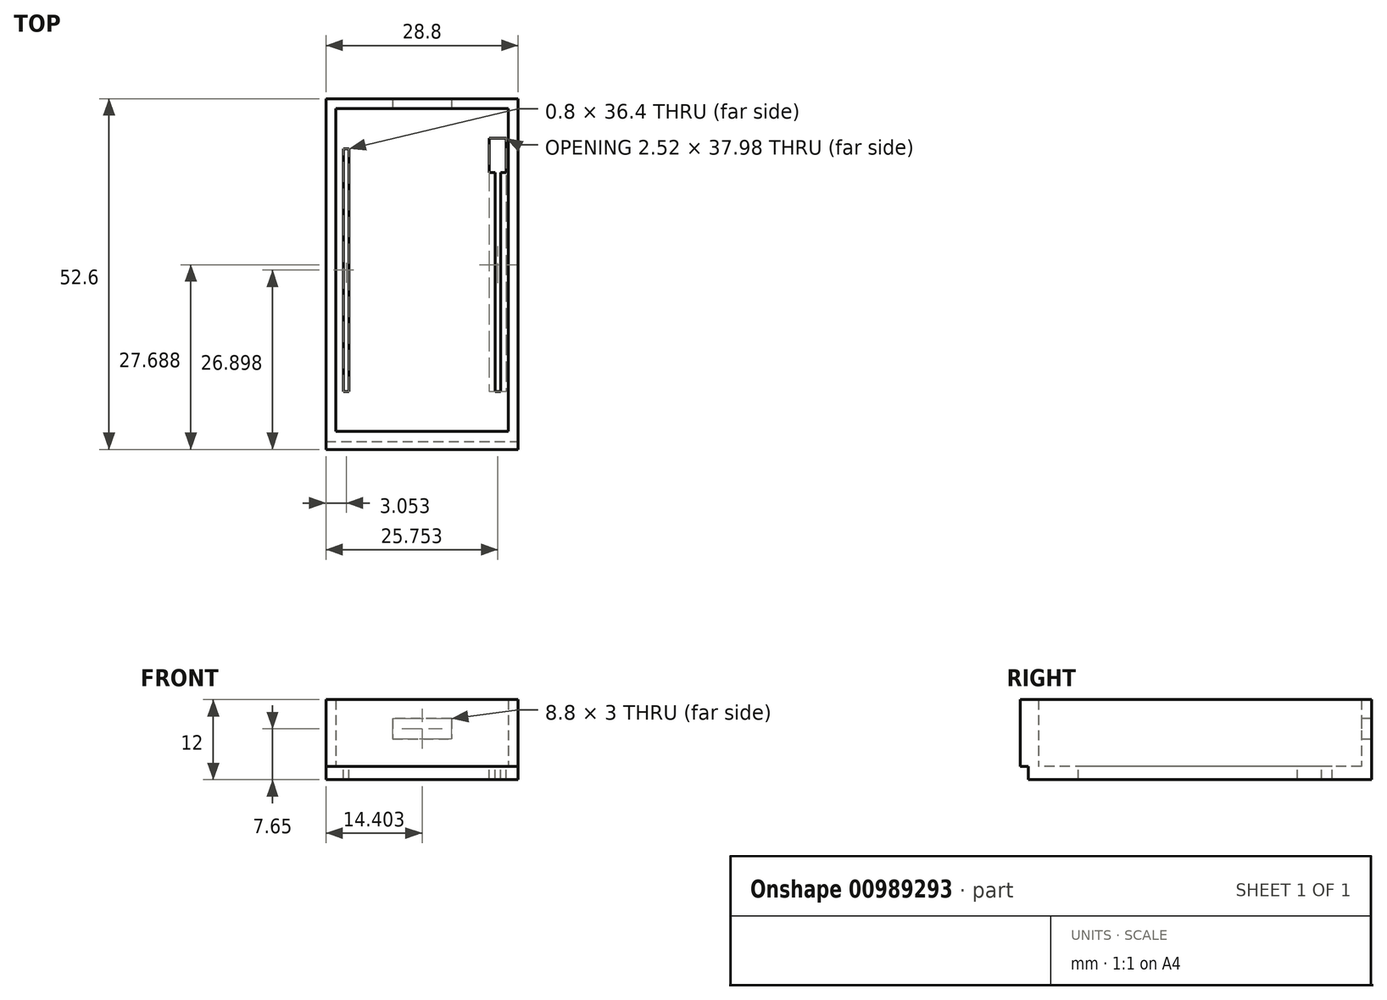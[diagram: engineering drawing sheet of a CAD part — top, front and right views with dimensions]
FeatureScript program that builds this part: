
annotation { "Feature Type Name" : "Feature", "Feature Type Description" : "" }
export const myFeature = defineFeature(function(context is Context, id is Id, definition is map)
    precondition{}
    {
        {
            var Q0;
            Q0=qCreatedBy(makeId("Top.planeOp"),FACE);
            var sketch = newSketch(context, id + "F0", { "sketchPlane" : qUnion([Q0])});
            skLineSegment(sketch, "E0.bottom", {"start": v(-15.5, 31.2) * mm, "end": v(10.3, 31.2) * mm});
            skLineSegment(sketch, "E0.top", {"start": v(-15.5, -17.2) * mm, "end": v(10.3, -17.2) * mm});
            skLineSegment(sketch, "E0.left", {"start": v(-15.5, 31.2) * mm, "end": v(-15.5, -17.2) * mm});
            skLineSegment(sketch, "E0.right", {"start": v(10.3, 31.2) * mm, "end": v(10.3, -17.2) * mm});
            skLineSegment(sketch, "E1.0", {"start": v(-17, 32.7) * mm, "end": v(11.8, 32.7) * mm});
            skLineSegment(sketch, "E1.1", {"start": v(-17, 32.7) * mm, "end": v(-17, -18.7) * mm});
            skLineSegment(sketch, "E1.2", {"start": v(-17, -18.7) * mm, "end": v(11.8, -18.7) * mm});
            skLineSegment(sketch, "E1.3", {"start": v(11.8, 32.7) * mm, "end": v(11.8, -18.7) * mm});
            skPoint(sketch, "E2", {"position": v(-2.6, 31.2) * mm});
            skPoint(sketch, "E3", {"position": v(-2.6, 32.7) * mm});
            skLineSegment(sketch, "E4", {"start": v(-2.6, 32.7) * mm, "end": v(-2.6, 31.2) * mm, "construction": true});
            skPoint(sketch, "E5", {"position": v(-2.6, 31.95) * mm});
            skLineSegment(sketch, "E6.bottom", {"start": v(1.8, 31.2) * mm, "end": v(-7, 31.2) * mm});
            skLineSegment(sketch, "E6.top", {"start": v(1.8, 32.7) * mm, "end": v(-7, 32.7) * mm});
            skLineSegment(sketch, "E6.left", {"start": v(1.8, 31.2) * mm, "end": v(1.8, 32.7) * mm});
            skLineSegment(sketch, "E6.right", {"start": v(-7, 31.2) * mm, "end": v(-7, 32.7) * mm});
            skLineSegment(sketch, "E7", {"start": v(-13.96, 31.2) * mm, "end": v(-13.96, -17.2) * mm, "construction": true});
            skLineSegment(sketch, "E8", {"start": v(8.74, 31.2) * mm, "end": v(8.74, -17.2) * mm, "construction": true});
            skLineSegment(sketch, "E9", {"start": v(-15.5, 31.2) * mm, "end": v(-13.96, 31.2) * mm, "construction": true});
            skLineSegment(sketch, "E10", {"start": v(8.74, 31.2) * mm, "end": v(10.3, 31.2) * mm, "construction": true});
            skPoint(sketch, "E11", {"position": v(-13.96, 7) * mm});
            skPoint(sketch, "E12", {"position": v(8.74, 7) * mm});
            skLineSegment(sketch, "E13.bottom", {"start": v(-14.36, 25.2) * mm, "end": v(-13.56, 25.2) * mm});
            skLineSegment(sketch, "E13.top", {"start": v(-14.36, -11.2) * mm, "end": v(-13.56, -11.2) * mm});
            skLineSegment(sketch, "E13.left", {"start": v(-14.36, 25.2) * mm, "end": v(-14.36, -11.2) * mm});
            skLineSegment(sketch, "E13.right", {"start": v(-13.56, 25.2) * mm, "end": v(-13.56, -11.2) * mm});
            skLineSegment(sketch, "E14.bottom", {"start": v(8.34, 25.2) * mm, "end": v(9.14, 25.2) * mm});
            skLineSegment(sketch, "E14.top", {"start": v(8.34, -11.2) * mm, "end": v(9.14, -11.2) * mm});
            skLineSegment(sketch, "E14.left", {"start": v(8.34, 25.2) * mm, "end": v(8.34, -11.2) * mm});
            skLineSegment(sketch, "E14.right", {"start": v(9.14, 25.2) * mm, "end": v(9.14, -11.2) * mm});
            skPoint(sketch, "E15", {"position": v(-2.6, -18.7) * mm});
            skPoint(sketch, "E16", {"position": v(-13.96, 25.2) * mm});
            skPoint(sketch, "E17", {"position": v(8.74, 25.2) * mm});
            skPoint(sketch, "E18", {"position": v(-13.96, -11.2) * mm});
            skPoint(sketch, "E19", {"position": v(8.74, -11.2) * mm});
            skPoint(sketch, "E20", {"position": v(8.74, 26.78) * mm});
            skPoint(sketch, "E21", {"position": v(8.74, 21.6) * mm});
            skLineSegment(sketch, "E22", {"start": v(8.74, 26.78) * mm, "end": v(7.48, 26.78) * mm});
            skLineSegment(sketch, "E23", {"start": v(7.48, 26.78) * mm, "end": v(8.74, 26.78) * mm});
            skLineSegment(sketch, "E24", {"start": v(8.74, 26.78) * mm, "end": v(10, 26.78) * mm});
            skLineSegment(sketch, "E25.bottom", {"start": v(7.48, 26.78) * mm, "end": v(10, 26.78) * mm});
            skLineSegment(sketch, "E25.top", {"start": v(7.48, 21.6) * mm, "end": v(10, 21.6) * mm});
            skLineSegment(sketch, "E25.left", {"start": v(7.48, 26.78) * mm, "end": v(7.48, 21.6) * mm});
            skLineSegment(sketch, "E25.right", {"start": v(10, 26.78) * mm, "end": v(10, 21.6) * mm});
            skLineSegment(sketch, "E26.top", {"start": v(-17, -19.9) * mm, "end": v(11.8, -19.9) * mm});
            skLineSegment(sketch, "E26.left", {"start": v(-17, -18.7) * mm, "end": v(-17, -19.9) * mm});
            skLineSegment(sketch, "E26.right", {"start": v(11.8, -18.7) * mm, "end": v(11.8, -19.9) * mm});
            skSolve(sketch);
        }
        {
            var Q0;
            Q0=makeQuery(id+"F0.imprint","IMPRINT",FACE,{"disambiguationData":[TD([[makeQuery(id+"F0.imprint","IMPRINT",EDGE,{"derivedFrom":sQuery(id+"F0.wireOp",EDGE,"E0.top")}),-1.0]])]});
            var Q1;
            Q1=makeQuery(id+"F0.imprint","IMPRINT",FACE,{"disambiguationData":[TD([[makeQuery(id+"F0.imprint","IMPRINT",EDGE,{"derivedFrom":sQuery(id+"F0.wireOp",EDGE,"E0.top")}),1.0]])]});
            var Q2;
            {var subQ2=sQuery(id+"F0.wireOp",EDGE,"E6.left");Q2=makeQuery(id+"F0.imprint","IMPRINT",FACE,{"disambiguationData":[TD([[makeQuery(id+"F0.imprint","IMPRINT",EDGE,{"derivedFrom":subQ2}),1.0]])]});}
            extrude(context, id + "F1", {"entities" : qUnion([Q0, Q1, Q2]), "oppositeDirection" : true, "depth" : 2 * mm, "offsetDistance" : 25 * mm});
        }
        {
            var Q0;
            Q0=makeQuery(id+"F0.imprint","IMPRINT",FACE,{"disambiguationData":[TD([[makeQuery(id+"F0.imprint","IMPRINT",EDGE,{"derivedFrom":sQuery(id+"F0.wireOp",EDGE,"E0.top")}),-1.0]])]});
            extrude(context, id + "F2", {"entities" : qUnion([Q0]), "operationType" : NewBodyOperationType.ADD, "depth" : 10 * mm, "offsetDistance" : 25 * mm});
        }
        {
            var Q0;
            {var subQ2=sQuery(id+"F0.wireOp",EDGE,"E6.left");Q0=makeQuery(id+"F0.imprint","IMPRINT",FACE,{"disambiguationData":[TD([[makeQuery(id+"F0.imprint","IMPRINT",EDGE,{"derivedFrom":subQ2}),1.0]])]});}
            extrude(context, id + "F3", {"entities" : qUnion([Q0]), "operationType" : NewBodyOperationType.ADD, "depth" : 4.15 * mm, "offsetDistance" : 25 * mm});
        }
        {
            var Q0;
            Q0=makeQuery(id+"F0.imprint","IMPRINT",FACE,{"disambiguationData":[TD([[makeQuery(id+"F0.imprint","IMPRINT",EDGE,{"derivedFrom":sQuery(id+"F0.wireOp",EDGE,"E13.bottom")}),-1.0]])]});
            var Q1;
            {var subQ0=sQuery(id+"F0.wireOp",EDGE,"E14.bottom");Q1=makeQuery(id+"F0.imprint","IMPRINT",FACE,{"disambiguationData":[TD([[makeQuery(id+"F0.imprint","IMPRINT",EDGE,{"derivedFrom":subQ0}),-1.0]])]});}
            extrude(context, id + "F4", {"entities" : qUnion([Q0, Q1]), "operationType" : NewBodyOperationType.REMOVE, "oppositeDirection" : true, "depth" : 2 * mm, "offsetDistance" : 25 * mm});
        }
        {
            var Q0;
            Q0=makeQuery(id+"F2.opExtrude","SWEPT_FACE",FACE,{"disambiguationData":[OSD([sQuery(id+"F0.wireOp",EDGE,"E6.right")])]});
            var sketch = newSketch(context, id + "F5", { "sketchPlane" : qUnion([Q0])});
            skPoint(sketch, "E27", {"position": v(32.7, 4.15) * mm});
            skPoint(sketch, "E28", {"position": v(31.2, 4.15) * mm});
            skPoint(sketch, "E29", {"position": v(31.2, 7.15) * mm});
            skPoint(sketch, "E30", {"position": v(32.7, 7.15) * mm});
            skLineSegment(sketch, "E31", {"start": v(31.2, 4.15) * mm, "end": v(31.2, 7.15) * mm});
            skLineSegment(sketch, "E32", {"start": v(32.7, 7.15) * mm, "end": v(31.2, 7.15) * mm});
            skLineSegment(sketch, "E33", {"start": v(32.7, 4.15) * mm, "end": v(32.7, 7.15) * mm});
            skLineSegment(sketch, "E34", {"start": v(32.7, 4.15) * mm, "end": v(31.2, 4.15) * mm});
            skLineSegment(sketch, "E35.bottom", {"start": v(31.2, 10) * mm, "end": v(32.7, 10) * mm});
            skLineSegment(sketch, "E35.top", {"start": v(31.2, 7.15) * mm, "end": v(32.7, 7.15) * mm});
            skLineSegment(sketch, "E35.left", {"start": v(31.2, 10) * mm, "end": v(31.2, 7.15) * mm});
            skLineSegment(sketch, "E35.right", {"start": v(32.7, 10) * mm, "end": v(32.7, 7.15) * mm});
            skSolve(sketch);
        }
        {
            var Q0;
            Q0=makeQuery(id+"F5.imprint","IMPRINT",FACE,{"disambiguationData":[TD([[makeQuery(id+"F5.imprint","IMPRINT",EDGE,{"derivedFrom":sQuery(id+"F5.wireOp",EDGE,"E35.bottom")}),-1.0]])]});
            extrude(context, id + "F6", {"entities" : qUnion([Q0]), "operationType" : NewBodyOperationType.ADD, "depth" : 8.8 * mm, "offsetDistance" : 25 * mm});
        }
        {
            var Q0;
            Q0=makeQuery(id+"F0.imprint","IMPRINT",FACE,{"disambiguationData":[TD([[makeQuery(id+"F0.imprint","IMPRINT",EDGE,{"derivedFrom":sQuery(id+"F0.wireOp",EDGE,"E1.2")}),-1.0]])]});
            extrude(context, id + "F7", {"entities" : qUnion([Q0]), "operationType" : NewBodyOperationType.ADD, "depth" : 10 * mm, "offsetDistance" : 25 * mm});
        }
    });
